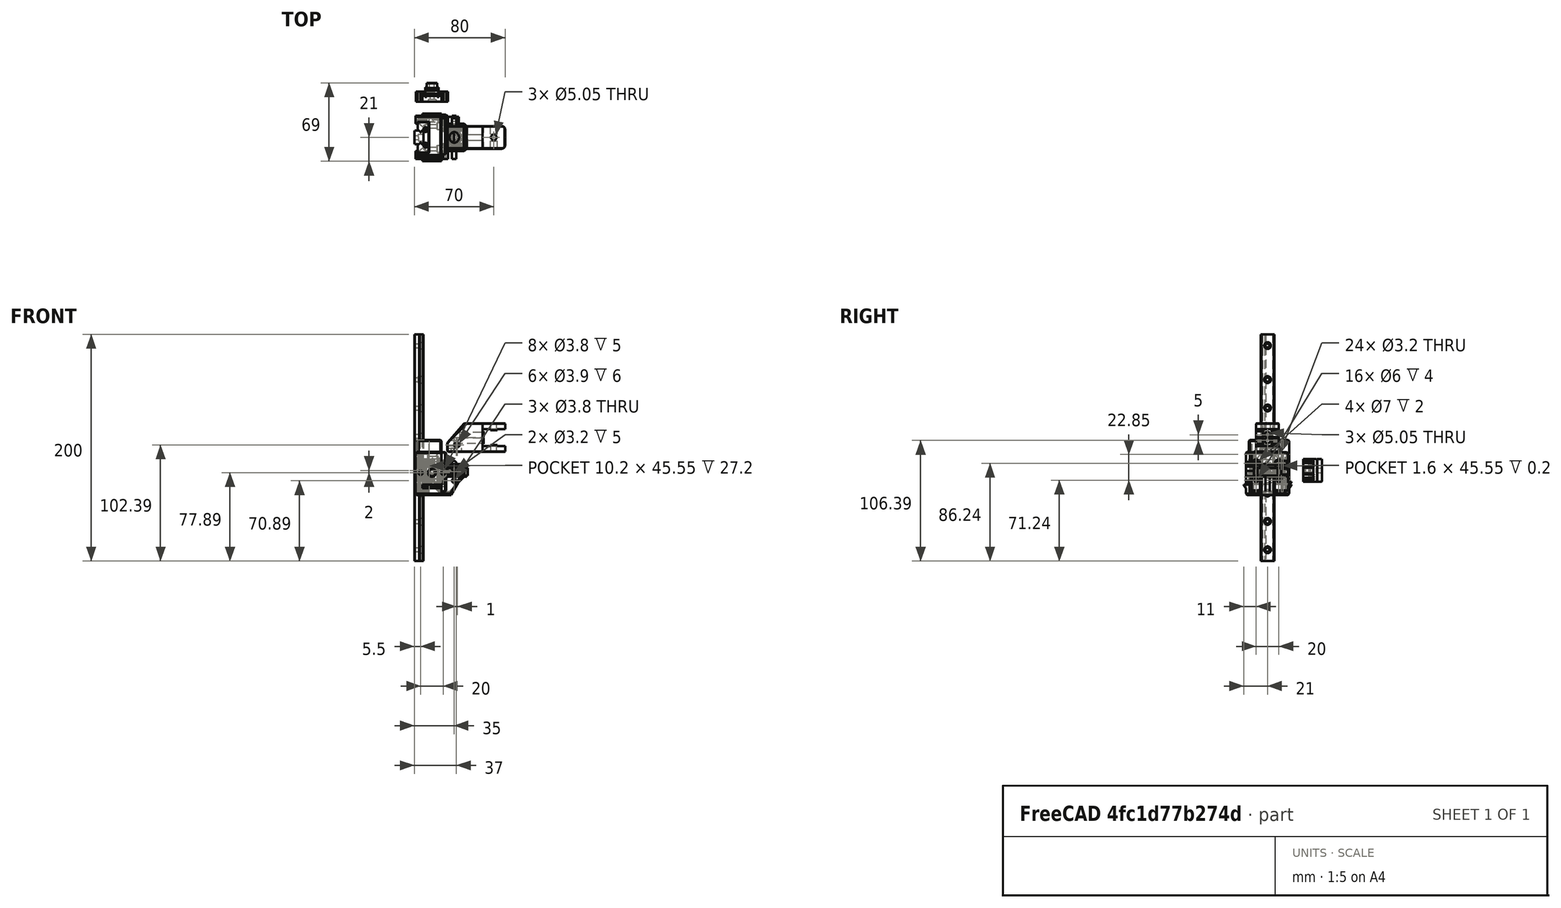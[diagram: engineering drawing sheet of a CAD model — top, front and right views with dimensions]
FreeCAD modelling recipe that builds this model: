
FCSTD DOCUMENT  (FreeCAD 0.19R24291 (Git))
Label: z-arm-mod-mgn12
License: Other
LicenseURL: GPL3
objects: Part::Box×31, Part::Feature×25, Part::MultiFuse×25, Part::Cylinder×23, Part::Chamfer×23, Part::Cut×16, Part::Refine×4, Part::Fillet×2, Part::Mirroring×1
note: 150 computed .brp shape members not serialized (recipe doc carries the construction recipe); baked Part::Feature solids carry a one-line shape summary decoded from their .brp

FEATURE [Part::Feature] Cut028005001  label="x-slider001"
  Placement = pos=(10,0,0) rot=(0,0,1;0rad)
  shape: bbox 34 x 35 x 34.7 mm, 82 faces (baked)
FEATURE [Part::Box] Box  label="Cube"
  AttacherType = Attacher::AttachEngine3D
  Height = 38
  Length = 11
  Placement = pos=(0,-16.5,-3) rot=(0,0,1;0rad)
  Width = 33
FEATURE [Part::Feature] Fusion001001  label="_MGN12-pref"
  Placement = pos=(-7.5,4e-15,38.61) rot=(0,0,-1;1.5708rad)
  shape: bbox 13 x 27 x 200 mm, 427 faces (baked)
FEATURE [Part::Cylinder] Cylinder
  Angle = 360
  AttacherType = Attacher::AttachEngine3D
  Height = 11
  Placement = pos=(-3.9e-15,0,17.35) rot=(0,1,0;1.5708rad)
  Radius = 1.6
FEATURE [Part::Cylinder] Cylinder001
  Angle = 360
  AttacherType = Attacher::AttachEngine3D
  Height = 4
  Placement = pos=(7,0,17.35) rot=(0,1,0;1.5708rad)
  Radius = 3
FEATURE [Part::Box] Box001  label="Cube001"
  AttacherType = Attacher::AttachEngine3D
  Height = 38
  Length = 11
  Placement = pos=(-10,-16.5,-3) rot=(0,0,1;0rad)
  Width = 2.9
FEATURE [Part::Box] Box002  label="Cube002"
  AttacherType = Attacher::AttachEngine3D
  Height = 38
  Length = 23
  Placement = pos=(-12,13.6,-3) rot=(0,0,1;0rad)
  Width = 5.4
FEATURE [Part::MultiFuse] Fusion
  Placement = pos=(0,10,-4.65) rot=(0,0,1;0rad)
  Shapes = -> [Cylinder001,Cylinder]
FEATURE [Part::Feature] Fusion001002  label="Fusion001"
  Placement = pos=(0,-10,-4.65) rot=(0,0,1;0rad)
  shape: bbox 11 x 6 x 6 mm, 6 faces (baked)
FEATURE [Part::Feature] Fusion001003  label="Fusion002"
  Placement = pos=(0,10,10.35) rot=(0,0,1;0rad)
  shape: bbox 11 x 6 x 6 mm, 6 faces (baked)
FEATURE [Part::Feature] Fusion001004  label="Fusion003"
  Placement = pos=(0,-10,10.35) rot=(0,0,1;0rad)
  shape: bbox 11 x 6 x 6 mm, 6 faces (baked)
FEATURE [Part::Box] Box003  label="Cube003"
  AttacherType = Attacher::AttachEngine3D
  Height = 38
  Length = 1.8
  Placement = pos=(-12,12,-3) rot=(0,0,1;0rad)
  Width = 2
FEATURE [Part::Box] Box004  label="Cube004"
  AttacherType = Attacher::AttachEngine3D
  Height = 7
  Length = 10
  Placement = pos=(6.5,13.5,15) rot=(0,0,1;0rad)
  Width = 5.5
FEATURE [Part::Feature] Cut028006001  label="y-slider001"
  Placement = pos=(10,0,0) rot=(0,0,1;0rad)
  shape: bbox 36 x 35 x 34.7 mm, 80 faces (baked)
FEATURE [Part::Cylinder] Cylinder002
  Angle = 360
  AttacherType = Attacher::AttachEngine3D
  Height = 5
  Placement = pos=(12,14,17.5) rot=(-1,0,0;1.5708rad)
  Radius = 1.9
FEATURE [Part::Cylinder] Cylinder003
  Angle = 360
  AttacherType = Attacher::AttachEngine3D
  Height = 5
  Placement = pos=(-8,14,17.5) rot=(-1,0,0;1.5708rad)
  Radius = 1.9
FEATURE [Part::Box] Box005  label="Cube005"
  AttacherType = Attacher::AttachEngine3D
  Height = 15
  Length = 5.5
  Placement = pos=(10,13.5,11) rot=(0,0,1;0rad)
  Width = 5.5
FEATURE [Part::Cylinder] Cylinder004
  Angle = 360
  AttacherType = Attacher::AttachEngine3D
  Height = 5
  Placement = pos=(2,22,17.5) rot=(-1,0,0;1.5708rad)
  Radius = 3.5
FEATURE [Part::Chamfer] Chamfer004013007003
  Base = -> Cylinder004
  Edges = 1 edges r=0.5: [Edge3]
  Placement = pos=(0,-3.5,0) rot=(0,0,1;0rad)
FEATURE [Part::MultiFuse] Fusion001006
  Placement = pos=(0.5,0,-1) rot=(0,0,1;0rad)
  Shapes = -> [Chamfer004013007003,Cylinder002,Cylinder003]
FEATURE [Part::Box] Box006  label="Cube006"
  AttacherType = Attacher::AttachEngine3D
  Height = 3
  Length = 17
  Placement = pos=(-6,18,4.5) rot=(0,0,1;0rad)
  Width = 3
FEATURE [Part::Chamfer] Chamfer004013007006
  Base = -> Box006
  Edges = 1 edges r=2: [Edge11]
  Placement = pos=(0,0,-1.5) rot=(0,0,1;0rad)
FEATURE [Part::Feature] Fusion003001  label="belt-holder"
  Placement = pos=(2.5,44,18.5) rot=(1,0,0;1.5708rad)
  shape: bbox 12 x 7 x 20 mm, 88 faces (baked)
FEATURE [Part::Feature] Cut002001  label="belt-clamp-nut"
  Placement = pos=(2.5,51.5,18.5) rot=(-1,0,0;1.5708rad)
  shape: bbox 9 x 5 x 20 mm, 11 faces (baked)
FEATURE [Part::Box] Box008  label="Cube008"
  AttacherType = Attacher::AttachEngine3D
  Height = 2.85
  Length = 11
  Placement = pos=(-10,3.5,-3) rot=(0,0,1;0rad)
  Width = 11
FEATURE [Part::Box] Box009  label="Cube009"
  AttacherType = Attacher::AttachEngine3D
  Height = 2.85
  Length = 11
  Placement = pos=(-10,-14.5,-3) rot=(0,0,1;0rad)
  Width = 11
FEATURE [Part::Chamfer] Chamfer
  Base = -> Box009
  Edges = 1 edges r=10: [Edge3]
FEATURE [Part::Chamfer] Chamfer004013007009
  Base = -> Box008
  Edges = 1 edges r=10: [Edge1]
FEATURE [Part::Box] Box010  label="Cube010"
  AttacherType = Attacher::AttachEngine3D
  Height = 2.85
  Length = 4
  Placement = pos=(-12,12,-3) rot=(0,0,1;0rad)
  Width = 2
FEATURE [Part::Box] Box011  label="Cube011"
  AttacherType = Attacher::AttachEngine3D
  Height = 8
  Length = 22
  Placement = pos=(11,-10,13) rot=(0,0,1;0rad)
  Width = 20
FEATURE [Part::Box] Box012  label="Cube012"
  AttacherType = Attacher::AttachEngine3D
  Height = 8
  Length = 20
  Placement = pos=(11,-12,13) rot=(0,0,1;0rad)
  Width = 24
FEATURE [Part::Feature] Fusion001  label="slider-slot"
  Placement = pos=(20,4e-15,19.5) rot=(0,0,-1;1.5708rad)
  shape: bbox 12.3 x 16.2 x 12.1 mm, 8 faces (baked)
FEATURE [Part::Feature] Fusion004005  label="slider-slot001"
  Placement = pos=(22,2,19.5) rot=(0,0,1;3.14159rad)
  shape: bbox 16.2 x 12.3 x 12.1 mm, 8 faces (baked)
FEATURE [Part::Chamfer] Chamfer004013007011012
  Base = -> Box011
  Edges = 2 edges r=3: [Edge5,Edge7]
FEATURE [Part::Box] Box015  label="Cube015"
  AttacherType = Attacher::AttachEngine3D
  Height = 19
  Length = 20
  Placement = pos=(9.5,-6.5,-3) rot=(0,0,1;0rad)
  Width = 13
FEATURE [Part::Chamfer] Chamfer004013007011015002
  Base = -> Box004
  Edges = 2 edges r=1: [Edge6,Edge8]
FEATURE [Part::Chamfer] Chamfer004013007011015004
  Base = -> Box005
  Edges = 2 edges r=4: [Edge6,Edge8]
FEATURE [Part::Box] Box016  label="Cube016"
  AttacherType = Attacher::AttachEngine3D
  Height = 20
  Length = 2
  Placement = pos=(10.5,13.5,8.5) rot=(0,0,1;0rad)
  Width = 5.5
FEATURE [Part::Feature] Defeatured003
  shape: bbox 28 x 9 x 20 mm, 43 faces (baked)
FEATURE [Part::Chamfer] Chamfer004013007011015006002  label="belt-connector-rf"
  Base = -> Defeatured003
  Edges = 4 edges r=1.5: [Edge18,Edge41,Edge42,Edge56]
FEATURE [Part::Chamfer] Chamfer004013007011015006003
  Base = -> Box016
  Edges = 2 edges r=1.5: [Edge6,Edge8]
FEATURE [Part::Feature] Cut028006004005001  label="block-base001"
  shape: bbox 28.5 x 37.5 x 48.4 mm, 58 faces (baked)
FEATURE [Part::Feature] Cut028006004005002  label="block-base002"
  shape: bbox 28.5 x 37.5 x 48.4 mm, 58 faces (baked)
FEATURE [Part::Cylinder] Cylinder005
  Angle = 360
  AttacherType = Attacher::AttachEngine3D
  Height = 5
  Radius = 6.55
FEATURE [Part::Cylinder] Cylinder006
  Angle = 360
  AttacherType = Attacher::AttachEngine3D
  Height = 2
  Placement = pos=(0,0,3) rot=(0,0,1;0rad)
  Radius = 2.65
FEATURE [Part::Box] Box017  label="Cube017"
  AttacherType = Attacher::AttachEngine3D
  Height = 25
  Length = 31
  Placement = pos=(16,-10,35) rot=(0,0,1;0rad)
  Width = 20
FEATURE [Part::Box] Box018  label="Cube018"
  AttacherType = Attacher::AttachEngine3D
  Height = 5
  Length = 20
  Placement = pos=(47,-10,35) rot=(0,0,1;0rad)
  Width = 20
FEATURE [Part::Box] Box019  label="Cube019"
  AttacherType = Attacher::AttachEngine3D
  Height = 5.9
  Length = 2
  Placement = pos=(46,-10,47) rot=(0,0,1;0rad)
  Width = 6
FEATURE [Part::Cylinder] Cylinder007
  Angle = 360
  AttacherType = Attacher::AttachEngine3D
  Height = 37
  Placement = pos=(14,0,50) rot=(0,1,0;1.5708rad)
  Radius = 2.525
FEATURE [Part::Chamfer] Chamfer004013007011015006005
  Base = -> Box017
  Edges = 1 edges: [Edge2 r1=17 r2=15]
FEATURE [Part::Box] Box020  label="Cube020"
  AttacherType = Attacher::AttachEngine3D
  Height = 5.9
  Length = 2
  Placement = pos=(46,4,47) rot=(0,0,1;0rad)
  Width = 6
FEATURE [Part::Cylinder] Cylinder008
  Angle = 360
  AttacherType = Attacher::AttachEngine3D
  Height = 13
  Placement = pos=(14,0,50) rot=(0,1,0;1.5708rad)
  Radius = 4.75
FEATURE [Part::Box] Box021  label="Cube021"
  AttacherType = Attacher::AttachEngine3D
  Height = 1
  Length = 6
  Placement = pos=(54,-10,40) rot=(0,0,1;0rad)
  Width = 7
FEATURE [Part::MultiFuse] Fusion004019
  Shapes = -> [Cylinder008,Cylinder007]
FEATURE [Part::Fillet] Fillet
  Base = -> Box018
  Edges = 2 edges r=3: [Edge5,Edge7]
FEATURE [Part::Cylinder] Cylinder009
  Angle = 360
  AttacherType = Attacher::AttachEngine3D
  Height = 10
  Placement = pos=(57,0,32) rot=(0,0,1;0rad)
  Radius = 2.525
FEATURE [Part::Box] Box022  label="Cube022"
  AttacherType = Attacher::AttachEngine3D
  Height = 1
  Length = 6
  Placement = pos=(54,3,40) rot=(0,0,1;0rad)
  Width = 7
FEATURE [Part::Box] Box023  label="Cube023"
  AttacherType = Attacher::AttachEngine3D
  Height = 10
  Length = 12
  Placement = pos=(7,-4,28) rot=(0,0,1;0rad)
  Width = 8
FEATURE [Part::Cut] Cut028006004005005
  Base = -> Cylinder005
  Placement = pos=(22,0,33) rot=(0,0,1;0rad)
  Tool = -> Cylinder006
FEATURE [Part::MultiFuse] Fusion004022
  Shapes = -> [Box023,Cut028006004005005]
FEATURE [Part::Cylinder] Cylinder011
  Angle = 360
  AttacherType = Attacher::AttachEngine3D
  Height = 10
  Placement = pos=(24,-4,41) rot=(1,0,0;1.5708rad)
  Radius = 1.95
FEATURE [Part::Cylinder] Cylinder012
  Angle = 360
  AttacherType = Attacher::AttachEngine3D
  Height = 10
  Placement = pos=(24,14,41) rot=(1,0,0;1.5708rad)
  Radius = 1.95
FEATURE [Part::MultiFuse] Fusion004023
  Shapes = -> [Cylinder011,Cylinder012]
FEATURE [Part::Cylinder] Cylinder014
  Angle = 360
  AttacherType = Attacher::AttachEngine3D
  Height = 10
  Placement = pos=(22,-9,25) rot=(1,0,0;1.5708rad)
  Radius = 1.9
FEATURE [Part::Cylinder] Cylinder015
  Angle = 360
  AttacherType = Attacher::AttachEngine3D
  Height = 10
  Placement = pos=(22,19,25) rot=(1,0,0;1.5708rad)
  Radius = 1.9
FEATURE [Part::MultiFuse] Fusion004018
  Shapes = -> [Box020,Box019]
FEATURE [Part::Chamfer] Chamfer004013007011015006006
  Base = -> Fusion004018
  Edges = 2 edges r=1: [Edge8,Edge20]
FEATURE [Part::MultiFuse] Fusion004020
  Shapes = -> [Box022,Fillet,Box021]
FEATURE [Part::Cut] Cut028006004005004
  Base = -> Fusion004020
  Tool = -> Cylinder009
FEATURE [Part::MultiFuse] Fusion004021
  Shapes = -> [Chamfer004013007011015006005,Chamfer004013007011015006006,Cut028006004005004]
FEATURE [Part::Cut] Cut028006004005006
  Base = -> Fusion004021
  Tool = -> Fusion004022
FEATURE [Part::Chamfer] Chamfer004013007011015006007
  Base = -> Cut028006004005006
  Edges = 2 edges r=1: [Edge3,Edge9]
FEATURE [Part::Cut] Cut028006004005007
  Base = -> Chamfer004013007011015006007
  Tool = -> Fusion004019
FEATURE [Part::Chamfer] Chamfer004013007011015006008
  Base = -> Cut028006004005007
  Edges = 17 edges r=0.4: [Edge1,Edge3,Edge5,Edge11,Edge12,Edge13,Edge14,Edge24,Edge25,Edge29,Edge30,Edge31,Edge52,Edge70,Edge78,Edge79,Edge80]
FEATURE [Part::Cut] Cut028006004005008  label="bed-frame-mounter-btm"
  Base = -> Chamfer004013007011015006008
  Tool = -> Fusion004023
FEATURE [Part::Cylinder] Cylinder016
  Angle = 360
  AttacherType = Attacher::AttachEngine3D
  Height = 5
  Radius = 6.55
FEATURE [Part::Cylinder] Cylinder017
  Angle = 360
  AttacherType = Attacher::AttachEngine3D
  Height = 2
  Placement = pos=(0,0,3) rot=(0,0,1;0rad)
  Radius = 2.65
FEATURE [Part::Cut] Cut028006004005015
  Base = -> Cylinder016
  Placement = pos=(22,0,33) rot=(0,0,1;0rad)
  Tool = -> Cylinder017
FEATURE [Part::Box] Box024  label="Cube024"
  AttacherType = Attacher::AttachEngine3D
  Height = 25
  Length = 31
  Placement = pos=(16,-10,35) rot=(0,0,1;0rad)
  Width = 20
FEATURE [Part::Box] Box025  label="Cube025"
  AttacherType = Attacher::AttachEngine3D
  Height = 5
  Length = 20
  Placement = pos=(47,-10,35) rot=(0,0,1;0rad)
  Width = 20
FEATURE [Part::Box] Box026  label="Cube026"
  AttacherType = Attacher::AttachEngine3D
  Height = 5.9
  Length = 2
  Placement = pos=(46,-10,47) rot=(0,0,1;0rad)
  Width = 6
FEATURE [Part::Cylinder] Cylinder018
  Angle = 360
  AttacherType = Attacher::AttachEngine3D
  Height = 37
  Placement = pos=(14,0,45) rot=(0,1,0;1.5708rad)
  Radius = 2.525
FEATURE [Part::Box] Box027  label="Cube027"
  AttacherType = Attacher::AttachEngine3D
  Height = 5.9
  Length = 2
  Placement = pos=(46,4,47) rot=(0,0,1;0rad)
  Width = 6
FEATURE [Part::MultiFuse] Fusion004032
  Placement = pos=(0,0,-5.1) rot=(0,0,1;0rad)
  Shapes = -> [Box027,Box026]
FEATURE [Part::Cylinder] Cylinder019
  Angle = 360
  AttacherType = Attacher::AttachEngine3D
  Height = 8
  Placement = pos=(14,0,45) rot=(0,1,0;1.5708rad)
  Radius = 4.75
FEATURE [Part::Box] Box028  label="Cube028"
  AttacherType = Attacher::AttachEngine3D
  Height = 1
  Length = 6
  Placement = pos=(54,-10,40) rot=(0,0,1;0rad)
  Width = 7
FEATURE [Part::Fillet] Fillet001
  Base = -> Box025
  Edges = 2 edges r=3: [Edge5,Edge7]
FEATURE [Part::Cylinder] Cylinder020
  Angle = 360
  AttacherType = Attacher::AttachEngine3D
  Height = 10
  Placement = pos=(57,0,32) rot=(0,0,1;0rad)
  Radius = 2.525
FEATURE [Part::Box] Box029  label="Cube029"
  AttacherType = Attacher::AttachEngine3D
  Height = 1
  Length = 6
  Placement = pos=(54,3,40) rot=(0,0,1;0rad)
  Width = 7
FEATURE [Part::Box] Box030  label="Cube030"
  AttacherType = Attacher::AttachEngine3D
  Height = 10
  Length = 12
  Placement = pos=(7,-4,28) rot=(0,0,1;0rad)
  Width = 8
FEATURE [Part::MultiFuse] Fusion004030
  Shapes = -> [Box030,Cut028006004005015]
FEATURE [Part::Cylinder] Cylinder021
  Angle = 360
  AttacherType = Attacher::AttachEngine3D
  Height = 10
  Placement = pos=(24,-4,41) rot=(1,0,0;1.5708rad)
  Radius = 1.95
FEATURE [Part::Cylinder] Cylinder022
  Angle = 360
  AttacherType = Attacher::AttachEngine3D
  Height = 10
  Placement = pos=(24,14,41) rot=(1,0,0;1.5708rad)
  Radius = 1.95
FEATURE [Part::MultiFuse] Fusion004031
  Placement = pos=(1,0,0) rot=(0,0,1;0rad)
  Shapes = -> [Cylinder021,Cylinder022]
FEATURE [Part::Cut] Cut028006004005016
  Base = -> Fillet001
  Placement = pos=(0,0,6) rot=(0,0,1;0rad)
  Tool = -> Cylinder020
FEATURE [Part::MultiFuse] Fusion004034
  Placement = pos=(0,0,14) rot=(0,0,1;0rad)
  Shapes = -> [Cut028006004005016,Box028,Box029]
FEATURE [Part::Chamfer] Chamfer004013007011015006009004
  Base = -> Fusion004032
  Edges = 2 edges r=1: [Edge6,Edge18]
  Placement = pos=(0,0,0.1) rot=(0,0,1;0rad)
FEATURE [Part::Cut] Cut028006004005017
  Base = -> Box024
  Tool = -> Fusion004030
FEATURE [Part::Chamfer] Chamfer004013007011015006009005
  Base = -> Cut028006004005017
  Edges = 1 edges r=17: [Edge1]
FEATURE [Part::MultiFuse] Fusion004035
  Shapes = -> [Cylinder019,Cylinder018]
FEATURE [Part::Cut] Cut028006004005018
  Base = -> Chamfer004013007011015006009005
  Tool = -> Fusion004035
FEATURE [Part::Chamfer] Chamfer004013007011015006009006
  Base = -> Cut028006004005018
  Edges = 2 edges r=1: [Edge2,Edge8]
FEATURE [Part::MultiFuse] Fusion004025002
  Placement = pos=(0,0,-5) rot=(0,0,1;0rad)
  Shapes = -> [Cylinder015,Cylinder014]
FEATURE [Part::MultiFuse] Fusion004025007
  Shapes = -> [Chamfer004013007011015006009006,Chamfer004013007011015006009004]
FEATURE [Part::Cut] Cut028006004005011003
  Base = -> Fusion004025007
  Tool = -> Fusion004031
FEATURE [Part::MultiFuse] Fusion004025008
  Shapes = -> [Fusion004034,Cut028006004005011003]
FEATURE [Part::Chamfer] Chamfer004013007011015006009007  label="bed-frame-mount-top"
  Base = -> Fusion004025008
  Edges = 15 edges r=0.4: [Edge1,Edge5,Edge6,Edge8,Edge9,Edge29,Edge31,Edge62,Edge63,Edge64,Edge65,Edge70,Edge76,Edge77,Edge78]
FEATURE [Part::Feature] Chamfer004013007011015006009007001001  label="bed-frame-mount-top002"
  shape: bbox 51 x 20 x 25 mm, 56 faces (baked)
FEATURE [Part::Cylinder] Cylinder013
  Angle = 360
  AttacherType = Attacher::AttachEngine3D
  Height = 10
  Placement = pos=(22,17,25) rot=(1,0,0;1.5708rad)
  Radius = 1.9
FEATURE [Part::Cylinder] Cylinder010
  Angle = 360
  AttacherType = Attacher::AttachEngine3D
  Height = 14
  Placement = pos=(22,7,9.5) rot=(1,0,0;1.5708rad)
  Radius = 1.9
FEATURE [Part::Chamfer] Chamfer004013007011015006009007001002  label="supporter-base"
  Base = -> Box015
  Edges = 1 edges: [Edge8 r1=17 r2=10]
FEATURE [Part::Chamfer] Chamfer004013007011015006009007001003
  Base = -> Chamfer004013007011015006009007001002
  Edges = 6 edges r=1: [Edge1,Edge3,Edge5,Edge8,Edge9,Edge13]
FEATURE [Part::Feature] Cut028006004005011004002  label="supporter-rf002"
  shape: bbox 20 x 13 x 19 mm, 14 faces (baked)
FEATURE [Part::Box] Box031  label="Cube031"
  AttacherType = Attacher::AttachEngine3D
  Height = 6.4
  Length = 9.5
  Placement = pos=(-2.25,37.7,15.3) rot=(0,0,1;0rad)
  Width = 8
FEATURE [Part::Cut] Cut028006004005011004003  label="belt-mounter-9mm"
  Base = -> Fusion003001
  Tool = -> Box031
FEATURE [Part::Refine] Cut028006004005011004003001  label="belt-mounter-9mm001"
  Source = -> Cut028006004005011004003
FEATURE [Part::Feature] Cut028006004005011004003001001  label="belt-mounter-9mm002"
  shape: bbox 12 x 7 x 20 mm, 80 faces (baked)
FEATURE [Part::Box] Box032  label="Cube032"
  AttacherType = Attacher::AttachEngine3D
  Height = 8
  Length = 22
  Placement = pos=(11,-12,16) rot=(0,0,1;0rad)
  Width = 24
FEATURE [Part::Chamfer] Chamfer004013007011015006009007001004
  Base = -> Box032
  Edges = 2 edges r=5: [Edge5,Edge7]
FEATURE [Part::Chamfer] Chamfer004013007011015006009007001005  label="extend-arm-base"
  Base = -> Chamfer004013007011015006009007001004
  Edges = 5 edges r=0.4: [Edge1,Edge5,Edge7,Edge8,Edge9]
FEATURE [Part::Feature] Fusion004025013  label="slider-slot002"
  Placement = pos=(24,4e-15,19.5) rot=(0,0,-1;1.5708rad)
  shape: bbox 12.3 x 16.2 x 12.1 mm, 8 faces (baked)
FEATURE [Part::Feature] Chamfer004013007011015006009007001005001  label="extend-arm-base001"
  shape: bbox 22 x 24 x 8 mm, 13 faces (baked)
FEATURE [Part::MultiFuse] Fusion004025014
  Shapes = -> [Fusion004025013,Fusion001]
FEATURE [Part::Cut] Cut028006004005011004003001002  label="x-arm"
  Base = -> Chamfer004013007011015006009007001005001
  Placement = pos=(0,0,-2.5) rot=(0,0,1;0rad)
  Tool = -> Fusion004025014
FEATURE [Part::Feature] Chamfer004013007011015006009007001005002  label="extend-arm-base002"
  shape: bbox 22 x 24 x 8 mm, 13 faces (baked)
FEATURE [Part::Feature] Fusion004005001  label="slider-slot003"
  Placement = pos=(22,-2,19.5) rot=(0,0,1;3.14159rad)
  shape: bbox 16.2 x 12.3 x 12.1 mm, 8 faces (baked)
FEATURE [Part::MultiFuse] Fusion004025016
  Shapes = -> [Fusion004005,Fusion004005001]
FEATURE [Part::Cut] Cut028006004005011004003001003  label="y-arm"
  Base = -> Chamfer004013007011015006009007001005002
  Placement = pos=(0,0,-2.5) rot=(0,0,1;0rad)
  Tool = -> Fusion004025016
FEATURE [Part::Box] Box033  label="Cube033"
  AttacherType = Attacher::AttachEngine3D
  Height = 8
  Length = 5.5
  Placement = pos=(11,10.5,16) rot=(0,0,1;0rad)
  Width = 3
FEATURE [Part::Chamfer] Chamfer004013007011015006009007001005003
  Base = -> Box033
  Edges = 1 edges r=3: [Edge6]
FEATURE [Part::Feature] Chamfer004013007011015006009007001005003001
  Placement = pos=(0,0,-2.5) rot=(0,0,1;0rad)
  shape: bbox 5.5 x 3 x 8 mm, 7 faces (baked)
FEATURE [Part::MultiFuse] Fusion004025020
  Shapes = -> [Box,Box002,Box003,Box001,Chamfer004013007009,Box010,Chamfer]
FEATURE [Part::MultiFuse] Fusion004025021
  Placement = pos=(0,0,-2.85) rot=(0,0,1;0rad)
  Shapes = -> [Fusion001002,Fusion001003,Fusion001004,Fusion]
FEATURE [Part::Cut] Cut  label="block-base-mgn12c"
  Base = -> Fusion004025020
  Tool = -> Fusion004025021
FEATURE [Part::Refine] Cut028006004005011004003001004  label="block-base-mgn12c001"
  Source = -> Cut
FEATURE [Part::Chamfer] Chamfer004013007011015006009007001005003002  label="block-base-mgn12-chamfer"
  Base = -> Cut028006004005011004003001004
  Edges = 12 edges r=1: [Edge1,Edge3,Edge5,Edge6,Edge12,Edge13,Edge58,Edge59,Edge60,Edge61,Edge62,Edge64]
FEATURE [Part::MultiFuse] Fusion004025022
  Placement = pos=(0,0,-2.5) rot=(0,0,1;0rad)
  Shapes = -> [Chamfer004013007011015006003,Chamfer004013007011015004,Chamfer004013007011015002]
FEATURE [Part::MultiFuse] Fusion004025023
  Shapes = -> [Chamfer004013007006,Fusion004025022,Chamfer004013007011015006009007001005003001]
FEATURE [Part::MultiFuse] Fusion004025024
  Shapes = -> [Chamfer004013007011015006009007001005003002,Fusion004025023]
FEATURE [Part::Cut] Cut028006004005011004003001005  label="mgn12c-block-mount"
  Base = -> Fusion004025024
  Tool = -> Fusion001006
FEATURE [Part::Cut] Cut028006004005011004003001006  label="supporter"
  Base = -> Chamfer004013007011015006009007001003
  Tool = -> Cylinder010
FEATURE [Part::Feature] Cut028006004005011004003001006001  label="supporter001"
  shape: bbox 20 x 13 x 19 mm, 14 faces (baked)
FEATURE [Part::Feature] Cut028006004005011004003001005001  label="mgn12c-block-mount001"
  shape: bbox 28.5 x 37.5 x 38 mm, 98 faces (baked)
FEATURE [Part::MultiFuse] Fusion004025025  label="y-slider-mgn12c"
  Shapes = -> [Cut028006004005011004003001003,Cut028006004005011004003001006001,Cut028006004005011004003001005001]
FEATURE [Part::Feature] Cut028006004005011004003001006002  label="supporter002"
  shape: bbox 20 x 13 x 19 mm, 14 faces (baked)
FEATURE [Part::Feature] Cut028006004005011004003001005002  label="mgn12c-block-mount002"
  shape: bbox 28.5 x 37.5 x 38 mm, 98 faces (baked)
FEATURE [Part::MultiFuse] Fusion004025026  label="x-slider-mgn12c"
  Shapes = -> [Cut028006004005011004003001002,Cut028006004005011004003001006002,Cut028006004005011004003001005002]
FEATURE [Part::Refine] Fusion004025026001  label="x-slider-mgn12c001"
  Source = -> Fusion004025026
FEATURE [Part::Refine] Fusion004025025001  label="y-slider-mgn12c001"
  Source = -> Fusion004025025
FEATURE [Part::Mirroring] Part__Mirroring  label="x-slider-mgn12c001 (Mirror #1)"
  Base = (0,0,0)
  Normal = (0,1,0)
  Source = -> Fusion004025026001
